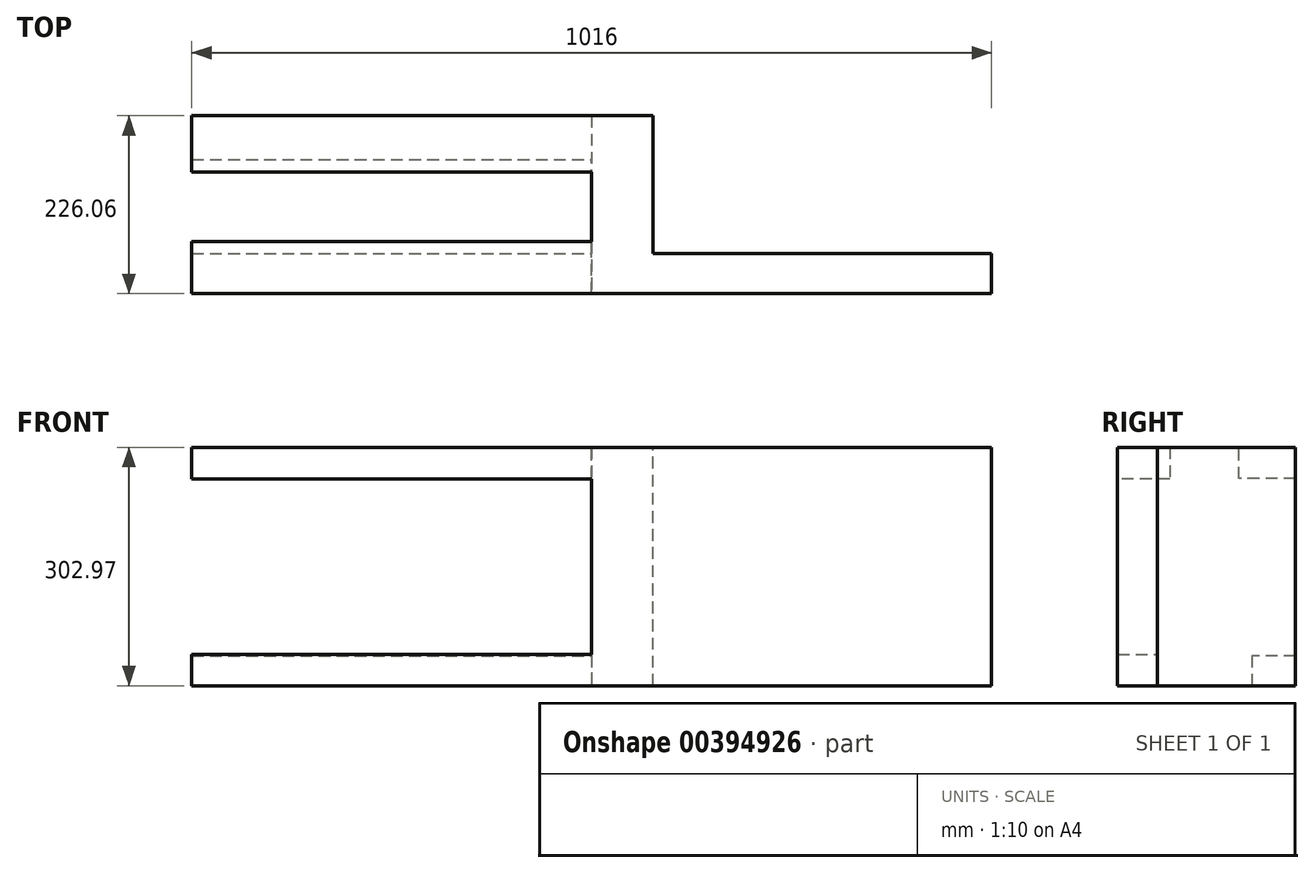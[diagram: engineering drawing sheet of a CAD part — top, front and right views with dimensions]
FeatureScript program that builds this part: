
annotation { "Feature Type Name" : "Feature", "Feature Type Description" : "" }
export const myFeature = defineFeature(function(context is Context, id is Id, definition is map)
    precondition{}
    {
        {
            var Q0;
            Q0=qCreatedBy(makeId("Front.planeOp"),FACE);
            var sketch = newSketch(context, id + "F0", { "sketchPlane" : qUnion([Q0])});
            skLineSegment(sketch, "E0.bottom", {"start": v(0, 0) * mm, "end": v(-508, 0) * mm});
            skLineSegment(sketch, "E0.top", {"start": v(0, 302.97) * mm, "end": v(-508, 302.97) * mm});
            skLineSegment(sketch, "E0.left", {"start": v(0, 0) * mm, "end": v(0, 302.97) * mm});
            skLineSegment(sketch, "E0.right", {"start": v(-508, 0) * mm, "end": v(-508, 302.97) * mm});
            skSolve(sketch);
        }
        {
            var Q0;
            Q0 = qSketchRegion(id + "F0", true);
            extrude(context, id + "F1", {"entities" : qUnion([Q0]), "depth" : 50.8 * mm});
        }
        {
            var Q0;
            Q0=makeQuery(id+"F1.opExtrude","CAP_FACE",FACE,{"disambiguationData":[OSD([sQuery(id+"F0.wireOp",EDGE,"E0.bottom"),sQuery(id+"F0.wireOp",EDGE,"E0.top"),sQuery(id+"F0.wireOp",EDGE,"E0.left"),sQuery(id+"F0.wireOp",EDGE,"E0.right")])],"isStart":true});
            var sketch = newSketch(context, id + "F2", { "sketchPlane" : qUnion([Q0])});
            skLineSegment(sketch, "E1.bottom", {"start": v(430.46, 0) * mm, "end": v(508, 0) * mm});
            skLineSegment(sketch, "E1.top", {"start": v(430.46, 302.97) * mm, "end": v(508, 302.97) * mm});
            skLineSegment(sketch, "E1.left", {"start": v(430.46, 0) * mm, "end": v(430.46, 302.97) * mm});
            skLineSegment(sketch, "E1.right", {"start": v(508, 0) * mm, "end": v(508, 302.97) * mm});
            skSolve(sketch);
        }
        {
            var Q0;
            Q0=makeQuery(id+"F2.imprint","IMPRINT",FACE,{"disambiguationData":[TD([[makeQuery(id+"F2.imprint","IMPRINT",EDGE,{"derivedFrom":sQuery(id+"F2.wireOp",EDGE,"E1.bottom")}),1.0]])]});
            extrude(context, id + "F3", {"entities" : qUnion([Q0]), "operationType" : NewBodyOperationType.ADD, "depth" : 175.26 * mm});
        }
        {
            var Q0;
            Q0=makeQuery(id+"F3.boolean.opBoolean","MERGE",FACE,{"derivedFrom":[makeQuery(id+"F1.opExtrude","SWEPT_FACE",FACE,{"disambiguationData":[OSD([sQuery(id+"F0.wireOp",EDGE,"E0.right")])]}),makeQuery(id+"F3.opExtrude","SWEPT_FACE",FACE,{"disambiguationData":[OSD([sQuery(id+"F2.wireOp",EDGE,"E1.right")])]})]});
            var sketch = newSketch(context, id + "F4", { "sketchPlane" : qUnion([Q0])});
            skLineSegment(sketch, "E2.bottom", {"start": v(-175.26, 263.16) * mm, "end": v(-103.47, 263.16) * mm});
            skLineSegment(sketch, "E2.top", {"start": v(-175.26, 302.97) * mm, "end": v(-103.47, 302.97) * mm});
            skLineSegment(sketch, "E2.left", {"start": v(-175.26, 263.16) * mm, "end": v(-175.26, 302.97) * mm});
            skLineSegment(sketch, "E2.right", {"start": v(-103.47, 263.16) * mm, "end": v(-103.47, 302.97) * mm});
            skLineSegment(sketch, "E3.bottom", {"start": v(-15.49, 302.97) * mm, "end": v(50.8, 302.97) * mm});
            skLineSegment(sketch, "E3.top", {"start": v(-15.49, 262.74) * mm, "end": v(50.8, 262.74) * mm});
            skLineSegment(sketch, "E3.left", {"start": v(-15.49, 302.97) * mm, "end": v(-15.49, 262.74) * mm});
            skLineSegment(sketch, "E3.right", {"start": v(50.8, 302.97) * mm, "end": v(50.8, 262.74) * mm});
            skLineSegment(sketch, "E4.bottom", {"start": v(50.8, 39.8) * mm, "end": v(0, 39.8) * mm});
            skLineSegment(sketch, "E4.top", {"start": v(50.8, 0) * mm, "end": v(0, 0) * mm});
            skLineSegment(sketch, "E4.left", {"start": v(50.8, 39.8) * mm, "end": v(50.8, 0) * mm});
            skLineSegment(sketch, "E4.right", {"start": v(0, 39.8) * mm, "end": v(0, 0) * mm});
            skLineSegment(sketch, "E5.bottom", {"start": v(-175.26, 38.11) * mm, "end": v(-119.97, 38.11) * mm});
            skLineSegment(sketch, "E5.top", {"start": v(-175.26, 0) * mm, "end": v(-119.97, 0) * mm});
            skLineSegment(sketch, "E5.left", {"start": v(-175.26, 38.11) * mm, "end": v(-175.26, 0) * mm});
            skLineSegment(sketch, "E5.right", {"start": v(-119.97, 38.11) * mm, "end": v(-119.97, 0) * mm});
            skSolve(sketch);
        }
        {
            var Q0;
            Q0=makeQuery(id+"F4.imprint","IMPRINT",FACE,{"disambiguationData":[TD([[makeQuery(id+"F4.imprint","IMPRINT",EDGE,{"derivedFrom":sQuery(id+"F4.wireOp",EDGE,"E2.bottom")}),1.0]])]});
            var Q1;
            Q1=makeQuery(id+"F4.imprint","IMPRINT",FACE,{"disambiguationData":[TD([[makeQuery(id+"F4.imprint","IMPRINT",EDGE,{"derivedFrom":sQuery(id+"F4.wireOp",EDGE,"E4.bottom")}),1.0]])]});
            var Q2;
            Q2=makeQuery(id+"F4.imprint","IMPRINT",FACE,{"disambiguationData":[TD([[makeQuery(id+"F4.imprint","IMPRINT",EDGE,{"derivedFrom":sQuery(id+"F4.wireOp",EDGE,"E5.bottom")}),-1.0]])]});
            var Q3;
            Q3=makeQuery(id+"F4.imprint","IMPRINT",FACE,{"disambiguationData":[TD([[makeQuery(id+"F4.imprint","IMPRINT",EDGE,{"derivedFrom":sQuery(id+"F4.wireOp",EDGE,"E3.bottom")}),1.0]])]});
            extrude(context, id + "F5", {"entities" : qUnion([Q0, Q1, Q2, Q3]), "operationType" : NewBodyOperationType.ADD, "depth" : 508 * mm});
        }
    });
